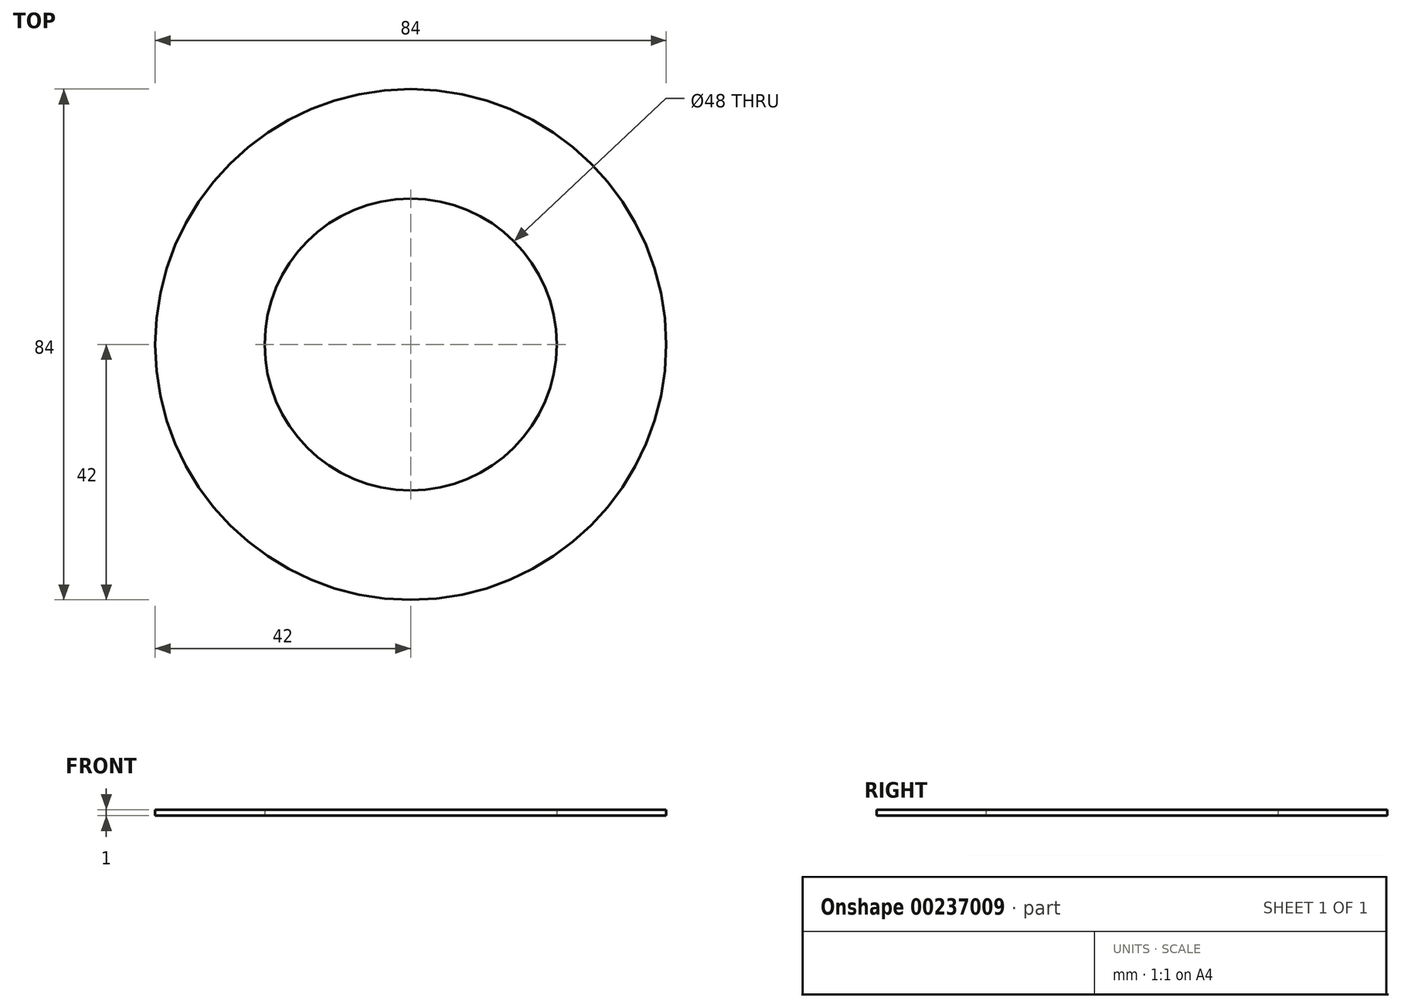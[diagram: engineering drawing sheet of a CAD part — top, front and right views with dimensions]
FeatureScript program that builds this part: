
annotation { "Feature Type Name" : "Feature", "Feature Type Description" : "" }
export const myFeature = defineFeature(function(context is Context, id is Id, definition is map)
    precondition{}
    {
        {
            var Q0;
            Q0=qCreatedBy(makeId("Front.planeOp"),FACE);
            var sketch = newSketch(context, id + "F0", { "sketchPlane" : qUnion([Q0])});
            skLineSegment(sketch, "E0", {"start": v(0, 0) * mm, "end": v(0, 27.86) * mm, "construction": true});
            skLineSegment(sketch, "E1.bottom", {"start": v(24, 4.96) * mm, "end": v(42, 4.96) * mm});
            skLineSegment(sketch, "E1.top", {"start": v(24, 3.96) * mm, "end": v(42, 3.96) * mm});
            skLineSegment(sketch, "E1.left", {"start": v(24, 4.96) * mm, "end": v(24, 3.96) * mm});
            skLineSegment(sketch, "E1.right", {"start": v(42, 4.96) * mm, "end": v(42, 3.96) * mm});
            skSolve(sketch);
        }
        {
            var Q0;
            Q0=makeQuery(id+"F0.imprint","IMPRINT",FACE,{"disambiguationData":[TD([[makeQuery(id+"F0.imprint","IMPRINT",EDGE,{"derivedFrom":sQuery(id+"F0.wireOp",EDGE,"E1.bottom")}),-1.0]])]});
            var Q1;
            Q1=sQuery(id+"F0.wireOp",EDGE,"E0");
            revolve(context, id + "F1", {"entities" : qUnion([Q0]), "axis" : qUnion([Q1]), "revolveType" : RevolveType.FULL});
        }
    });
